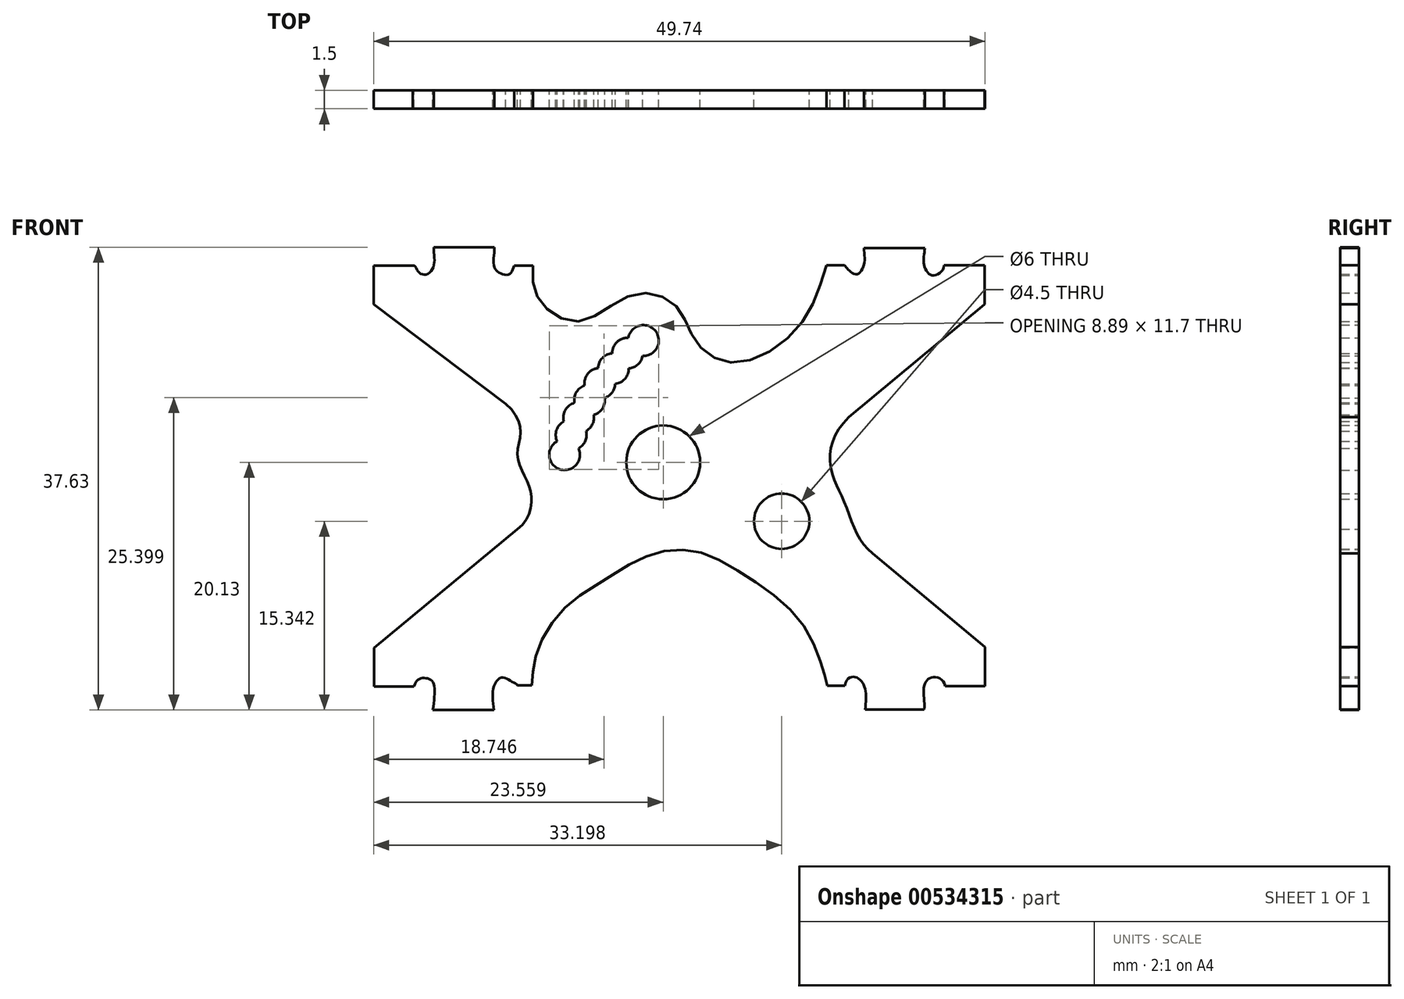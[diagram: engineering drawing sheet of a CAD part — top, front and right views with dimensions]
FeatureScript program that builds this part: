
annotation { "Feature Type Name" : "Feature", "Feature Type Description" : "" }
export const myFeature = defineFeature(function(context is Context, id is Id, definition is map)
    precondition{}
    {
        {
            var Q0;
            Q0=qCreatedBy(makeId("Front.planeOp"),FACE);
            var sketch = newSketch(context, id + "F0", { "sketchPlane" : qUnion([Q0])});
            skLineSegment(sketch, "E0", {"start": v(-19.95, 17.36) * mm, "end": v(-15.03, 17.36) * mm});
            skLineSegment(sketch, "E1", {"start": v(-13.4, 15.85) * mm, "end": v(-11.9, 15.85) * mm});
            skLineSegment(sketch, "E2", {"start": v(-24.85, 15.87) * mm, "end": v(-21.65, 15.87) * mm});
            skLineSegment(sketch, "E3", {"start": v(-24.85, 15.87) * mm, "end": v(-24.85, 12.7) * mm});
            skLineSegment(sketch, "E4", {"start": v(12, 15.9) * mm, "end": v(13.46, 15.9) * mm});
            skLineSegment(sketch, "E5", {"start": v(15.03, 17.3) * mm, "end": v(20, 17.3) * mm});
            skLineSegment(sketch, "E6", {"start": v(21.55, 15.88) * mm, "end": v(24.85, 15.88) * mm});
            skLineSegment(sketch, "E7", {"start": v(24.85, 15.88) * mm, "end": v(24.85, 12.7) * mm});
            skLineSegment(sketch, "E8", {"start": v(24.85, 12.7) * mm, "end": v(13.8, 3.53) * mm});
            skLineSegment(sketch, "E9", {"start": v(-24.85, 12.7) * mm, "end": v(-14.1, 4.62) * mm});
            skLineSegment(sketch, "E10", {"start": v(-21.55, -18.36) * mm, "end": v(-24.82, -18.36) * mm});
            skLineSegment(sketch, "E11", {"start": v(-24.82, -18.36) * mm, "end": v(-24.82, -15.24) * mm});
            skLineSegment(sketch, "E12", {"start": v(-24.82, -15.24) * mm, "end": v(-13.16, -5.58) * mm});
            skLineSegment(sketch, "E13", {"start": v(-20.03, -20.27) * mm, "end": v(-15.06, -20.27) * mm});
            skLineSegment(sketch, "E14", {"start": v(-11.97, -18.26) * mm, "end": v(-13.14, -18.26) * mm});
            skLineSegment(sketch, "E15", {"start": v(12.07, -18.3) * mm, "end": v(13.5, -18.3) * mm});
            skLineSegment(sketch, "E16", {"start": v(15.13, -20.23) * mm, "end": v(19.94, -20.23) * mm});
            skLineSegment(sketch, "E17", {"start": v(21.66, -18.33) * mm, "end": v(24.89, -18.33) * mm});
            skLineSegment(sketch, "E18", {"start": v(24.89, -18.33) * mm, "end": v(24.89, -15.17) * mm});
            skLineSegment(sketch, "E19", {"start": v(24.89, -15.17) * mm, "end": v(15.74, -7.55) * mm});
            skPoint(sketch, "E20", {"position": v(-1.3, 0) * mm});
            skPoint(sketch, "E21", {"position": v(8.35, -4.84) * mm});
            skPoint(sketch, "E22", {"position": v(-2.9, 9.77) * mm});
            skPoint(sketch, "E23", {"position": v(-4.19, 8.74) * mm});
            skPoint(sketch, "E24", {"position": v(-5.34, 7.48) * mm});
            skPoint(sketch, "E25", {"position": v(-6.44, 6.29) * mm});
            skPoint(sketch, "E26", {"position": v(-7.28, 4.92) * mm});
            skPoint(sketch, "E27", {"position": v(-8.17, 3.5) * mm});
            skPoint(sketch, "E28", {"position": v(-8.78, 2.1) * mm});
            skPoint(sketch, "E29", {"position": v(-9.3, 0.49) * mm});
            skCircle(sketch, "E30", {"center": v(-1.3, -0.14) * mm, "radius": 3 * mm});
            skCircle(sketch, "E31", {"center": v(8.35, -4.93) * mm, "radius": 2.25 * mm});
            skArc(sketch, "E32", {"start": v(-2.96, 8.52) * mm, "mid": v(-1.92, 10.55) * mm, "end": v(-4.13, 9.99) * mm});
            skArc(sketch, "E33", {"start": v(-4.13, 9.99) * mm, "mid": v(-5.06, 9.64) * mm, "end": v(-5.44, 8.73) * mm});
            skArc(sketch, "E34", {"start": v(-5.44, 8.73) * mm, "mid": v(-6.24, 8.35) * mm, "end": v(-6.59, 7.53) * mm});
            skArc(sketch, "E35", {"start": v(-6.59, 7.53) * mm, "mid": v(-7.44, 7.05) * mm, "end": v(-7.68, 6.1) * mm});
            skArc(sketch, "E36", {"start": v(-7.68, 6.1) * mm, "mid": v(-8.35, 5.56) * mm, "end": v(-8.5, 4.7) * mm});
            skArc(sketch, "E37", {"start": v(-8.5, 4.7) * mm, "mid": v(-9.25, 4.12) * mm, "end": v(-9.38, 3.19) * mm});
            skArc(sketch, "E38", {"start": v(-9.38, 3.19) * mm, "mid": v(-9.96, 2.49) * mm, "end": v(-9.92, 1.58) * mm});
            skArc(sketch, "E39", {"start": v(-9.92, 1.58) * mm, "mid": v(-9.7, -0.7) * mm, "end": v(-8.17, 1) * mm});
            skPoint(sketch, "E40", {"position": v(-20.63, 15.13) * mm});
            skPoint(sketch, "E41", {"position": v(-14.57, 15.25) * mm});
            skPoint(sketch, "E42", {"position": v(-11.2, 12.85) * mm});
            skPoint(sketch, "E43", {"position": v(-8, 11.34) * mm});
            skPoint(sketch, "E44", {"position": v(-3.87, 13.46) * mm});
            skPoint(sketch, "E45", {"position": v(-0.32, 12.66) * mm});
            skPoint(sketch, "E46", {"position": v(1.38, 9.68) * mm});
            skPoint(sketch, "E47", {"position": v(4.55, 7.97) * mm});
            skPoint(sketch, "E48", {"position": v(9.62, 10.77) * mm});
            skPoint(sketch, "E49", {"position": v(14.47, 15.16) * mm});
            skPoint(sketch, "E50", {"position": v(20.63, 15.07) * mm});
            skPoint(sketch, "E51", {"position": v(12.35, 1.04) * mm});
            skPoint(sketch, "E52", {"position": v(12.54, -1.33) * mm});
            skPoint(sketch, "E53", {"position": v(13.38, -3.22) * mm});
            skPoint(sketch, "E54", {"position": v(14.36, -5.73) * mm});
            skPoint(sketch, "E55", {"position": v(20.64, -17.62) * mm});
            skPoint(sketch, "E56", {"position": v(14.3, -17.6) * mm});
            skPoint(sketch, "E57", {"position": v(11.61, -16.64) * mm});
            skPoint(sketch, "E58", {"position": v(9.72, -12.85) * mm});
            skPoint(sketch, "E59", {"position": v(5.52, -9.42) * mm});
            skPoint(sketch, "E60", {"position": v(1.31, -7.36) * mm});
            skPoint(sketch, "E61", {"position": v(-2.54, -7.74) * mm});
            skPoint(sketch, "E62", {"position": v(-6.23, -9.8) * mm});
            skPoint(sketch, "E63", {"position": v(-9.63, -12.3) * mm});
            skPoint(sketch, "E64", {"position": v(-11.65, -15.9) * mm});
            skPoint(sketch, "E65", {"position": v(-14.38, -17.63) * mm});
            skPoint(sketch, "E66", {"position": v(-20.74, -17.68) * mm});
            skPoint(sketch, "E67", {"position": v(-12, -3.45) * mm});
            skPoint(sketch, "E68", {"position": v(-12.39, -1.62) * mm});
            skPoint(sketch, "E69", {"position": v(-13.14, 0.36) * mm});
            skPoint(sketch, "E70", {"position": v(-12.9, 2.3) * mm});
            skFitSpline(sketch, "E71", {"points": [v(-14.1, 4.62) * mm, v(-12.9, 2.3) * mm, v(-13.14, 0.36) * mm, v(-12.39, -1.62) * mm, v(-12, -3.45) * mm, v(-13.16, -5.58) * mm], "startDerivative": vector(12.13, -10.26) * mm, "endDerivative": vector(-10.89, -7.64) * mm});
            skFitSpline(sketch, "E72", {"points": [v(-21.55, -18.36) * mm, v(-20.74, -17.68) * mm, v(-20.03, -18) * mm, v(-20.03, -20.27) * mm], "startDerivative": vector(1.9, 5.9) * mm, "endDerivative": vector(-0.84, -5.97) * mm});
            skFitSpline(sketch, "E73", {"points": [v(-15.06, -20.27) * mm, v(-15.06, -18.36) * mm, v(-14.38, -17.63) * mm, v(-13.64, -17.95) * mm, v(-13.14, -18.26) * mm], "startDerivative": vector(-0.74, 5.84) * mm, "endDerivative": vector(1.36, -1.78) * mm});
            skFitSpline(sketch, "E74", {"points": [v(-11.97, -18.26) * mm, v(-11.65, -15.9) * mm, v(-9.63, -12.3) * mm, v(-6.23, -9.8) * mm, v(-2.54, -7.74) * mm, v(1.31, -7.36) * mm, v(5.52, -9.42) * mm, v(9.72, -12.85) * mm, v(11.61, -16.64) * mm, v(12.07, -18.3) * mm], "startDerivative": vector(0.88, 25.13) * mm, "endDerivative": vector(4.71, -19.69) * mm});
            skFitSpline(sketch, "E75", {"points": [v(13.5, -18.3) * mm, v(14.3, -17.6) * mm, v(15.08, -18.36) * mm, v(15.13, -20.23) * mm], "startDerivative": vector(0.94, 6.1) * mm, "endDerivative": vector(-0.59, -5) * mm});
            skFitSpline(sketch, "E76", {"points": [v(19.94, -20.23) * mm, v(19.94, -18.3) * mm, v(20.64, -17.62) * mm, v(21.66, -18.33) * mm], "startDerivative": vector(0.51, 5.23) * mm, "endDerivative": vector(1.1, -5.22) * mm});
            skFitSpline(sketch, "E77", {"points": [v(15.74, -7.55) * mm, v(14.36, -5.73) * mm, v(13.38, -3.22) * mm, v(12.54, -1.33) * mm, v(12.35, 1.04) * mm, v(13.8, 3.53) * mm], "startDerivative": vector(-9.76, 8.3) * mm, "endDerivative": vector(11.04, 11.08) * mm});
            skFitSpline(sketch, "E78", {"points": [v(21.55, 15.88) * mm, v(20.63, 15.07) * mm, v(19.94, 15.88) * mm, v(20, 17.3) * mm], "startDerivative": vector(-0.22, -4.67) * mm, "endDerivative": vector(0.4, 3.98) * mm});
            skFitSpline(sketch, "E79", {"points": [v(15.03, 17.3) * mm, v(15.03, 15.88) * mm, v(14.47, 15.16) * mm, v(13.8, 15.48) * mm, v(13.46, 15.9) * mm], "startDerivative": vector(0.57, -4.64) * mm, "endDerivative": vector(-1.43, 2.08) * mm});
            skFitSpline(sketch, "E80", {"points": [v(12, 15.9) * mm, v(9.62, 10.77) * mm, v(4.55, 7.97) * mm, v(1.38, 9.68) * mm, v(-0.32, 12.66) * mm, v(-3.87, 13.46) * mm, v(-8, 11.34) * mm, v(-11.2, 12.85) * mm, v(-11.9, 15.85) * mm], "startDerivative": vector(-11.17, -37.06) * mm, "endDerivative": vector(3.51, 32.85) * mm});
            skFitSpline(sketch, "E81", {"points": [v(-13.4, 15.85) * mm, v(-13.8, 15.16) * mm, v(-14.57, 15.25) * mm, v(-15.06, 15.85) * mm, v(-15.03, 17.36) * mm], "startDerivative": vector(-1.5, -3.62) * mm, "endDerivative": vector(-0.17, 5.1) * mm});
            skFitSpline(sketch, "E82", {"points": [v(-19.95, 17.36) * mm, v(-19.95, 15.85) * mm, v(-20.63, 15.13) * mm, v(-21.29, 15.47) * mm, v(-21.65, 15.87) * mm], "startDerivative": vector(0, -5.14) * mm, "endDerivative": vector(-3.74, -0.23) * mm});
            skArc(sketch, "E83.trimOffspring", {"start": v(-4.09, 7.5) * mm, "mid": v(-3.35, 7.81) * mm, "end": v(-2.96, 8.52) * mm});
            skArc(sketch, "E84.trimOffspring", {"start": v(-5.2, 6.24) * mm, "mid": v(-4.4, 6.66) * mm, "end": v(-4.09, 7.5) * mm});
            skArc(sketch, "E85.trimOffspring", {"start": v(-6.04, 5.1) * mm, "mid": v(-5.44, 5.54) * mm, "end": v(-5.2, 6.24) * mm});
            skArc(sketch, "E86.trimOffspring", {"start": v(-6.94, 3.72) * mm, "mid": v(-6.23, 4.24) * mm, "end": v(-6.04, 5.1) * mm});
            skArc(sketch, "E87.trimOffspring", {"start": v(-7.57, 2.4) * mm, "mid": v(-7.04, 2.96) * mm, "end": v(-6.94, 3.72) * mm});
            skArc(sketch, "E88.trimOffspring", {"start": v(-8.17, 1) * mm, "mid": v(-7.63, 1.6) * mm, "end": v(-7.57, 2.4) * mm});
            skSolve(sketch);
        }
        {
            var Q0;
            Q0=qSketchRegion(id+"F0",true);
            extrude(context, id + "F1", {"entities" : qUnion([Q0]), "depth" : 1.5 * mm});
        }
    });
